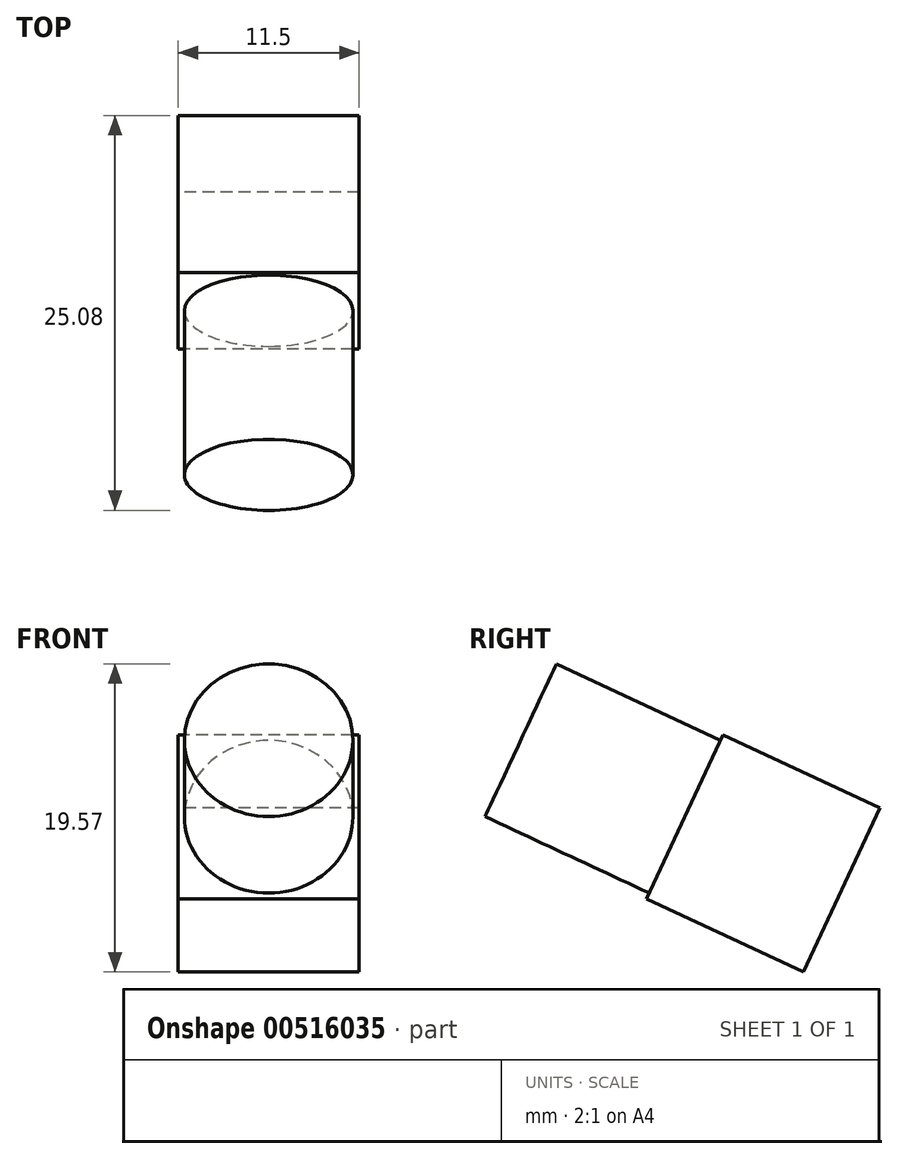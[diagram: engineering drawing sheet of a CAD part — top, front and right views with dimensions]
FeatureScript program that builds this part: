
annotation { "Feature Type Name" : "Feature", "Feature Type Description" : "" }
export const myFeature = defineFeature(function(context is Context, id is Id, definition is map)
    precondition{}
    {
        {
            var Q0;
            Q0=qCreatedBy(makeId("Right.planeOp"),FACE);
            var sketch = newSketch(context, id + "F0", { "sketchPlane" : qUnion([Q0])});
            skLineSegment(sketch, "E0", {"start": v(0, 0) * mm, "end": v(-9.97, 4.65) * mm});
            skLineSegment(sketch, "E1", {"start": v(-9.97, 4.65) * mm, "end": v(-5.1, 15.07) * mm});
            skLineSegment(sketch, "E2", {"start": v(-5.1, 15.07) * mm, "end": v(4.86, 10.42) * mm});
            skLineSegment(sketch, "E3", {"start": v(4.86, 10.42) * mm, "end": v(0, 0) * mm});
            skSolve(sketch);
        }
        {
            var Q0;
            Q0 = qSketchRegion(id + "F0", true);
            extrude(context, id + "F1", {"entities" : qUnion([Q0]), "endBound" : BoundingType.SYMMETRIC, "depth" : 11.5 * mm, "offsetDistance" : 25 * mm});
        }
        {
            var Q0;
            Q0=makeQuery(id+"F1.opExtrude","SWEPT_FACE",FACE,{"disambiguationData":[OSD([sQuery(id+"F0.wireOp",EDGE,"E1")])]});
            var sketch = newSketch(context, id + "F2", { "sketchPlane" : qUnion([Q0])});
            skLineSegment(sketch, "E4", {"start": v(5.75, 0) * mm, "end": v(-5.75, 11.5) * mm, "construction": true});
            skCircle(sketch, "E5", {"center": v(0, 5.75) * mm, "radius": 5.35 * mm});
            skSolve(sketch);
        }
        {
            var Q0;
            Q0 = qSketchRegion(id + "F2", true);
            extrude(context, id + "F3", {"entities" : qUnion([Q0]), "operationType" : NewBodyOperationType.ADD, "depth" : 11.5 * mm, "offsetDistance" : 25 * mm});
        }
    });
